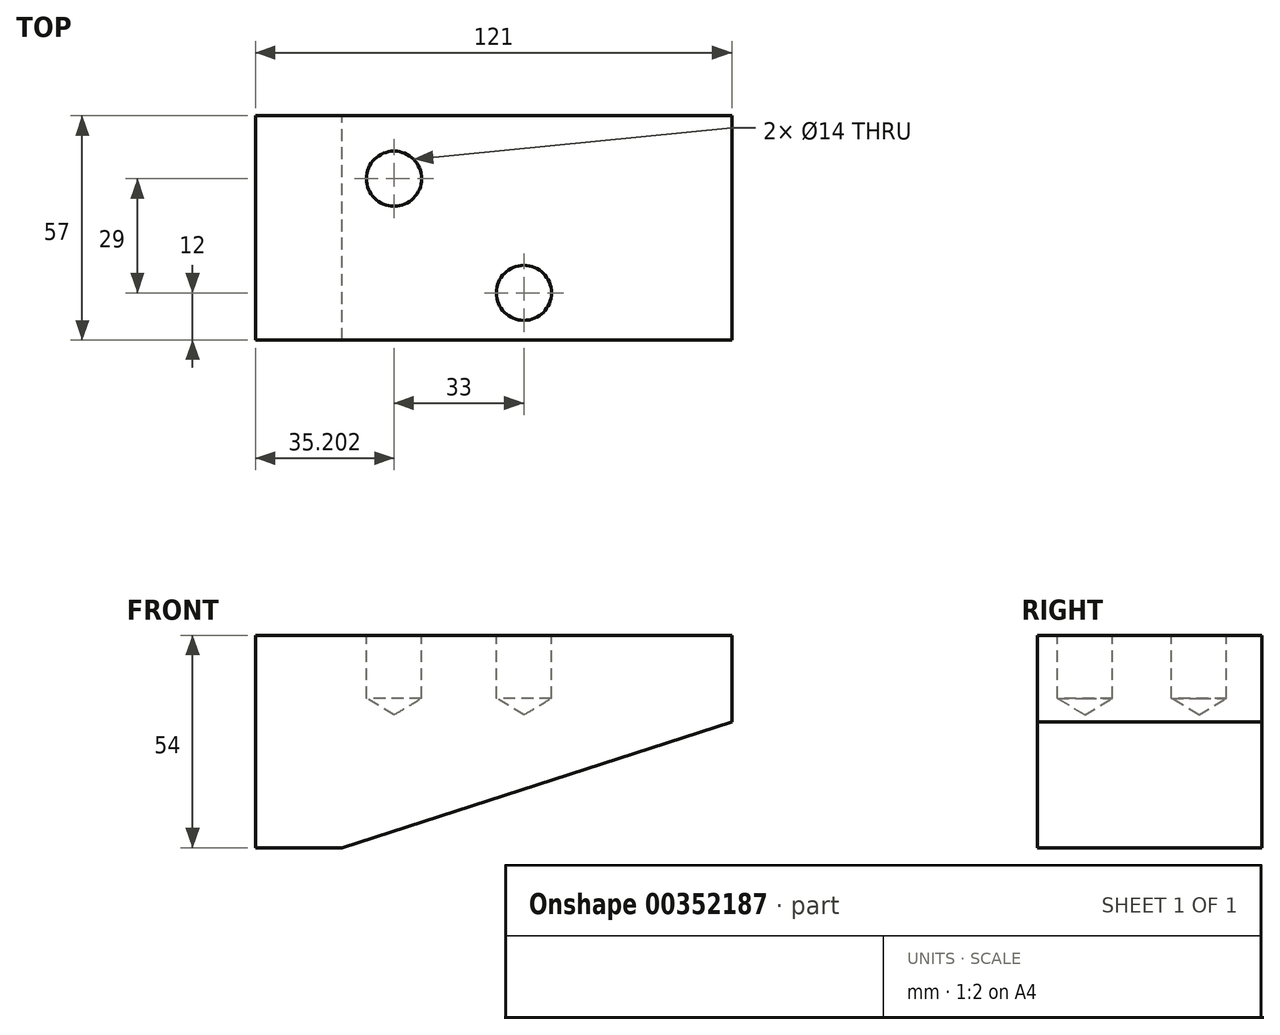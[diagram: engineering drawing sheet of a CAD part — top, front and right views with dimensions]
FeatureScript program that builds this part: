
annotation { "Feature Type Name" : "Feature", "Feature Type Description" : "" }
export const myFeature = defineFeature(function(context is Context, id is Id, definition is map)
    precondition{}
    {
        {
            var Q0;
            Q0=qCreatedBy(makeId("Front.planeOp"),FACE);
            var sketch = newSketch(context, id + "F0", { "sketchPlane" : qUnion([Q0])});
            skLineSegment(sketch, "E0", {"start": v(0, 54) * mm, "end": v(0, 0) * mm});
            skLineSegment(sketch, "E1", {"start": v(0, 0) * mm, "end": v(22, 0) * mm});
            skLineSegment(sketch, "E2", {"start": v(22, 0) * mm, "end": v(121, 32) * mm});
            skLineSegment(sketch, "E3", {"start": v(121, 32) * mm, "end": v(121, 54) * mm});
            skLineSegment(sketch, "E4", {"start": v(121, 54) * mm, "end": v(0, 54) * mm});
            skSolve(sketch);
        }
        {
            var Q0;
            Q0 = qSketchRegion(id + "F0", true);
            extrude(context, id + "F1", {"entities" : qUnion([Q0]), "depth" : 57 * mm});
        }
        {
            var Q0;
            Q0=makeQuery(id+"F1.opExtrude","SWEPT_FACE",FACE,{"disambiguationData":[OSD([sQuery(id+"F0.wireOp",EDGE,"E4")])]});
            var sketch = newSketch(context, id + "F2", { "sketchPlane" : qUnion([Q0])});
            skLineSegment(sketch, "E5", {"start": v(0, -11) * mm, "end": v(59, -57) * mm});
            skLineSegment(sketch, "E6", {"start": v(27.9, -32.75) * mm, "end": v(27.9, -57) * mm});
            skLineSegment(sketch, "E7", {"start": v(62, 0) * mm, "end": v(121, -46) * mm});
            skCircle(sketch, "E8", {"center": v(35.2, -16) * mm, "radius": 7 * mm});
            skCircle(sketch, "E9", {"center": v(68.2, -45) * mm, "radius": 7 * mm});
            skSolve(sketch);
        }
        {
            var Q0;
            Q0=sQuery(id+"F2.wireOp",VERTEX,"E8.center");
            var Q1;
            Q1=sQuery(id+"F2.wireOp",VERTEX,"E9.center");
            var Q2;
            Q2=makeQuery(id+"F1.opExtrude","SWEPT_BODY",BODY,{"disambiguationData":[OSD([sQuery(id+"F0.wireOp",EDGE,"E0"),sQuery(id+"F0.wireOp",EDGE,"E1"),sQuery(id+"F0.wireOp",EDGE,"E2"),sQuery(id+"F0.wireOp",EDGE,"E3"),sQuery(id+"F0.wireOp",EDGE,"E4")])]});
            hole(context, id + "F3", {"style" : HoleStyle.SIMPLE, "endStyle" : HoleEndStyle.BLIND, "holeDiameter" : 14 * mm, "holeDepth" : 16 * mm, "isTappedThrough" : true, "tappedDepth" : 12 * mm, "tapClearance" : 3, "locations" : qUnion([Q0, Q1]), "scope" : qUnion([Q2])});
        }
    });
